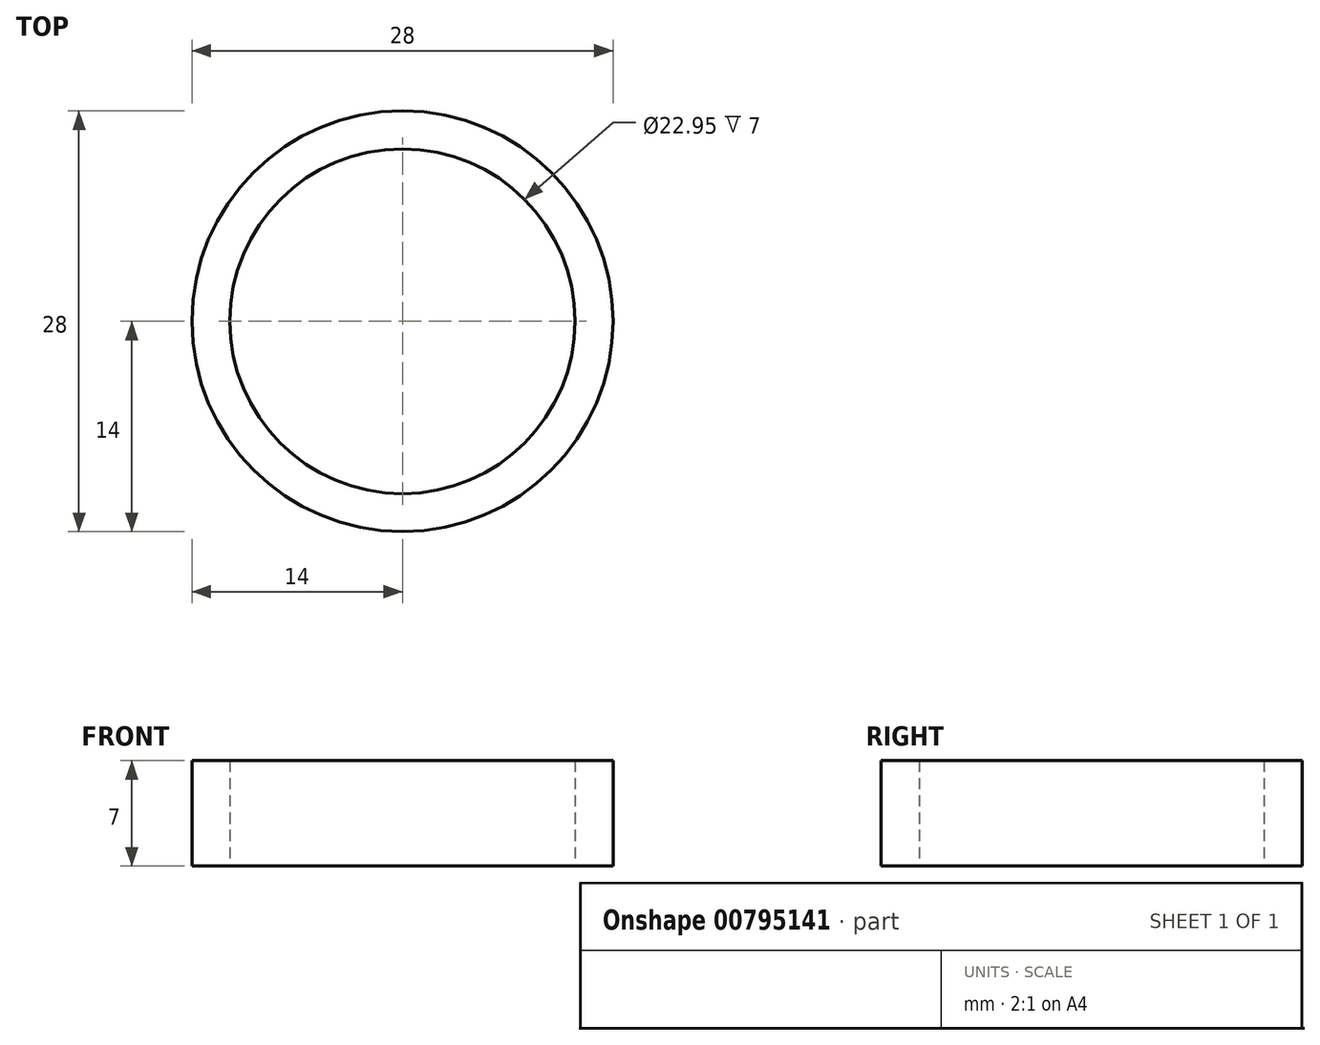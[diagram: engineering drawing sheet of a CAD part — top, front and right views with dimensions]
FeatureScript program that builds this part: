
annotation { "Feature Type Name" : "Feature", "Feature Type Description" : "" }
export const myFeature = defineFeature(function(context is Context, id is Id, definition is map)
    precondition{}
    {
        {
            var Q0;
            Q0=qCreatedBy(makeId("Top.planeOp"),FACE);
            var sketch = newSketch(context, id + "F0", { "sketchPlane" : qUnion([Q0])});
            skCircle(sketch, "E0", {"center": v(0, 0) * mm, "radius": 14 * mm});
            skCircle(sketch, "E1", {"center": v(0, 0) * mm, "radius": 11.47 * mm});
            skSolve(sketch);
        }
        {
            var Q0;
            Q0=makeQuery(id+"F0.imprint","IMPRINT",FACE,{"disambiguationData":[TD([[makeQuery(id+"F0.imprint","IMPRINT",EDGE,{"derivedFrom":sQuery(id+"F0.wireOp",EDGE,"E0")}),1.0]])]});
            extrude(context, id + "F1", {"entities" : qUnion([Q0]), "depth" : 7 * mm, "offsetDistance" : 25.4 * mm});
        }
    });
